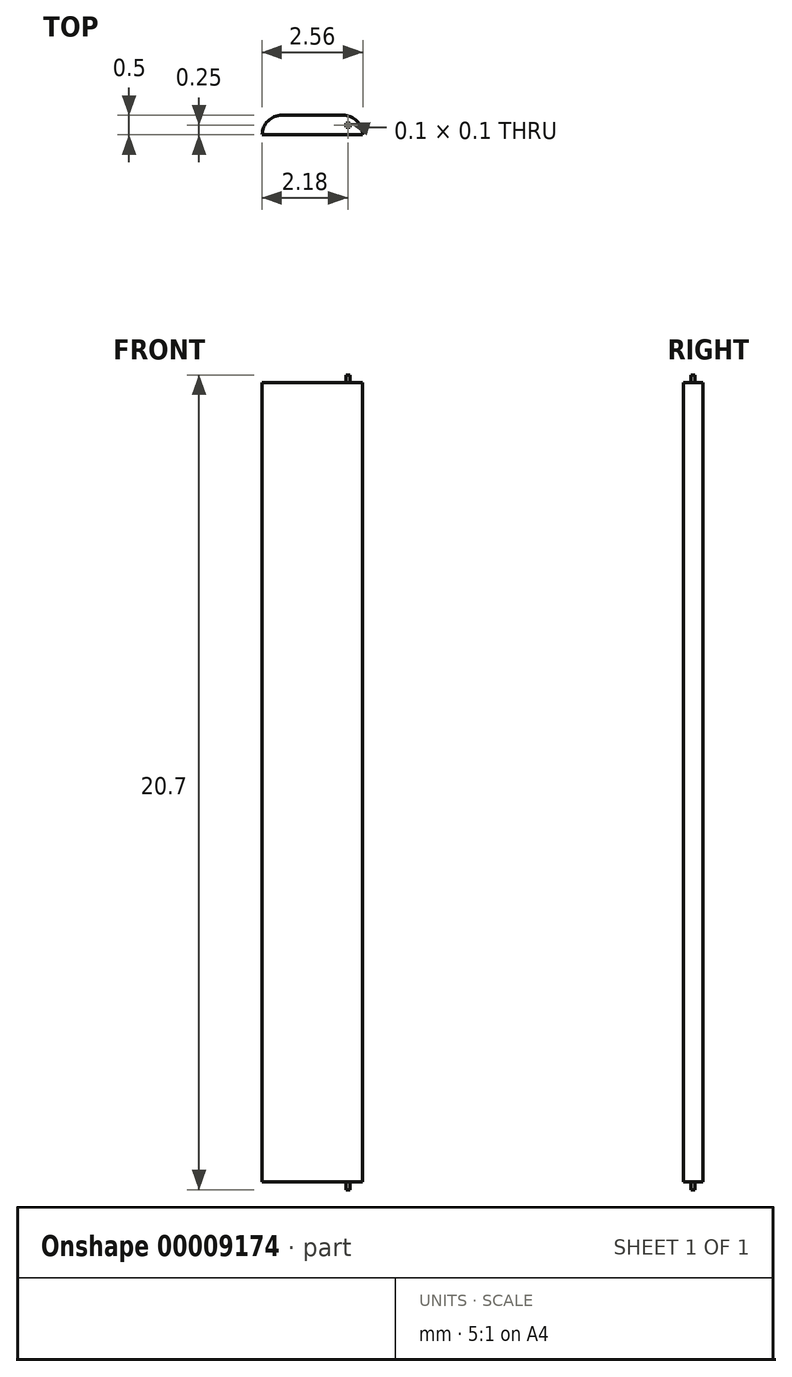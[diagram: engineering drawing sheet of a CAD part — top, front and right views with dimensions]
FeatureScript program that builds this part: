
annotation { "Feature Type Name" : "Feature", "Feature Type Description" : "" }
export const myFeature = defineFeature(function(context is Context, id is Id, definition is map)
    precondition{}
    {
        {
            var Q0;
            Q0=qCreatedBy(makeId("Top.planeOp"),FACE);
            var sketch = newSketch(context, id + "F0", { "sketchPlane" : qUnion([Q0])});
            skLineSegment(sketch, "E0.rect.bottom", {"start": v(1.28, 0.25) * mm, "end": v(-1.27, 0.25) * mm});
            skLineSegment(sketch, "E0.rect.top", {"start": v(1.27, -0.25) * mm, "end": v(-1.27, -0.25) * mm});
            skLineSegment(sketch, "E0.rect.left", {"start": v(1.27, 0.25) * mm, "end": v(1.27, -0.25) * mm});
            skLineSegment(sketch, "E0.rect.right", {"start": v(-1.27, 0.25) * mm, "end": v(-1.27, -0.25) * mm});
            skPoint(sketch, "E0.rect.middle", {"position": v(0, 0) * mm});
            skSolve(sketch);
        }
        {
            var Q0;
            Q0=makeQuery(id+"F0.imprint","IMPRINT",FACE,{"disambiguationData":[TD([[makeQuery(id+"F0.imprint","IMPRINT",EDGE,{"derivedFrom":sQuery(id+"F0.wireOp",EDGE,"E0.rect.bottom")}),1.0]])]});
            extrude(context, id + "F1", {"entities" : qUnion([Q0]), "depth" : 20.3 * mm});
        }
        {
            var Q0;
            Q0=makeQuery(id+"F1.opExtrude","SWEPT_EDGE",EDGE,{"disambiguationData":[OSD([sQuery(id+"F0.wireOp",EDGE,"E0.rect.bottom"),sQuery(id+"F0.wireOp",EDGE,"E0.rect.left")])]});
            var Q1;
            Q1=makeQuery(id+"F1.opExtrude","SWEPT_EDGE",EDGE,{"disambiguationData":[OSD([sQuery(id+"F0.wireOp",EDGE,"E0.rect.bottom"),sQuery(id+"F0.wireOp",EDGE,"E0.rect.right")])]});
            fillet(context, id + "F2", {"entities" : qUnion([Q0, Q1]), "radius" : 0.5 * mm, "tangentPropagation" : true, "allowEdgeOverflow" : false});
        }
        {
            var Q0;
            Q0=makeQuery(id+"F1.opExtrude","CAP_FACE",FACE,{"disambiguationData":[OSD([sQuery(id+"F0.wireOp",EDGE,"E0.rect.bottom"),sQuery(id+"F0.wireOp",EDGE,"E0.rect.top"),sQuery(id+"F0.wireOp",EDGE,"E0.rect.left"),sQuery(id+"F0.wireOp",EDGE,"E0.rect.right")])],"isStart":true});
            var sketch = newSketch(context, id + "F3", { "sketchPlane" : qUnion([Q0])});
            skLineSegment(sketch, "E1.rect.bottom", {"start": v(0.95, 0.05) * mm, "end": v(0.85, 0.05) * mm});
            skLineSegment(sketch, "E1.rect.top", {"start": v(0.95, -0.05) * mm, "end": v(0.85, -0.05) * mm});
            skLineSegment(sketch, "E1.rect.left", {"start": v(0.95, 0.05) * mm, "end": v(0.95, -0.05) * mm});
            skLineSegment(sketch, "E1.rect.right", {"start": v(0.85, 0.05) * mm, "end": v(0.85, -0.05) * mm});
            skPoint(sketch, "E1.rect.middle", {"position": v(0.9, 0) * mm});
            skSolve(sketch);
        }
        {
            var Q0;
            Q0=makeQuery(id+"F3.imprint","IMPRINT",FACE,{"disambiguationData":[TD([[makeQuery(id+"F3.imprint","IMPRINT",EDGE,{"derivedFrom":sQuery(id+"F3.wireOp",EDGE,"E1.rect.bottom")}),1.0]])]});
            extrude(context, id + "F4", {"entities" : qUnion([Q0]), "operationType" : NewBodyOperationType.ADD, "depth" : 0.2 * mm});
        }
        {
            var Q0;
            Q0=makeQuery(id+"F1.opExtrude","CAP_FACE",FACE,{"disambiguationData":[OSD([sQuery(id+"F0.wireOp",EDGE,"E0.rect.bottom"),sQuery(id+"F0.wireOp",EDGE,"E0.rect.top"),sQuery(id+"F0.wireOp",EDGE,"E0.rect.left"),sQuery(id+"F0.wireOp",EDGE,"E0.rect.right")])],"isStart":false});
            var sketch = newSketch(context, id + "F5", { "sketchPlane" : qUnion([Q0])});
            skLineSegment(sketch, "E2.rect.bottom", {"start": v(0.95, 0.05) * mm, "end": v(0.85, 0.05) * mm});
            skLineSegment(sketch, "E2.rect.top", {"start": v(0.95, -0.05) * mm, "end": v(0.85, -0.05) * mm});
            skLineSegment(sketch, "E2.rect.left", {"start": v(0.95, 0.05) * mm, "end": v(0.95, -0.05) * mm});
            skLineSegment(sketch, "E2.rect.right", {"start": v(0.85, 0.05) * mm, "end": v(0.85, -0.05) * mm});
            skPoint(sketch, "E2.rect.middle", {"position": v(0.9, 0) * mm});
            skSolve(sketch);
        }
        {
            var Q0;
            Q0=makeQuery(id+"F5.imprint","IMPRINT",FACE,{"disambiguationData":[TD([[makeQuery(id+"F5.imprint","IMPRINT",EDGE,{"derivedFrom":sQuery(id+"F5.wireOp",EDGE,"E2.rect.bottom")}),1.0]])]});
            extrude(context, id + "F6", {"entities" : qUnion([Q0]), "operationType" : NewBodyOperationType.ADD, "depth" : 0.2 * mm});
        }
    });
